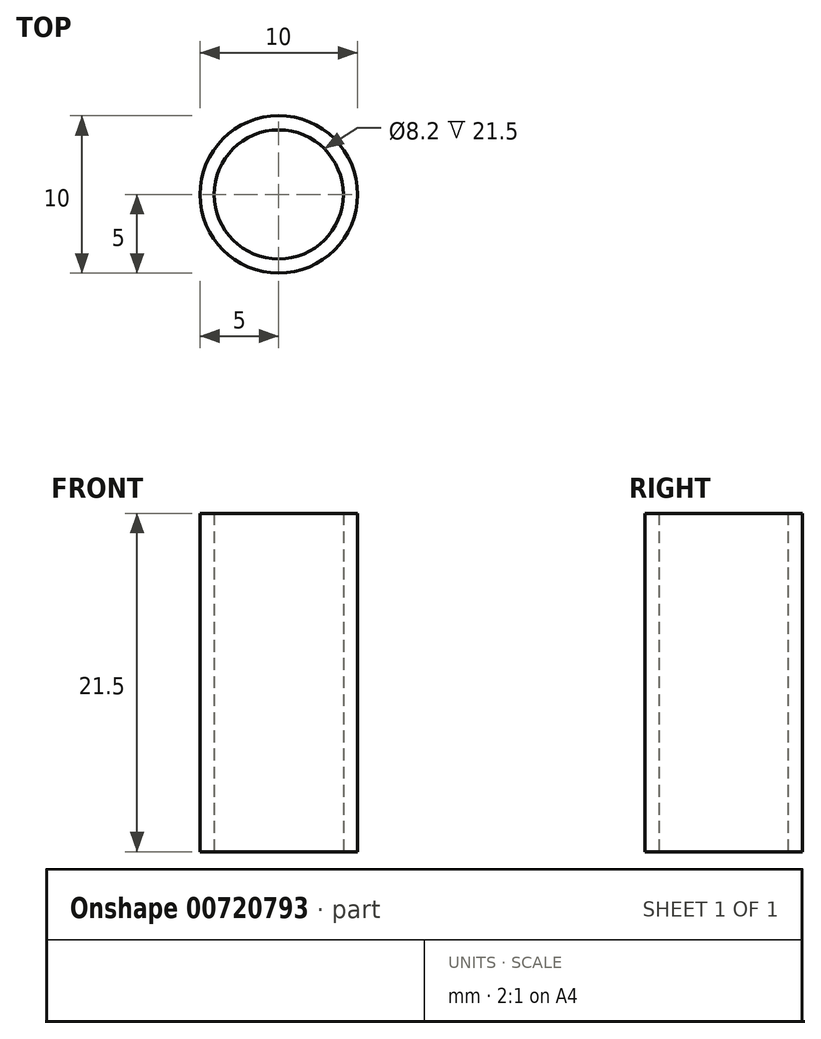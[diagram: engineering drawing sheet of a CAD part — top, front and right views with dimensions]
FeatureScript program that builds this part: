
annotation { "Feature Type Name" : "Feature", "Feature Type Description" : "" }
export const myFeature = defineFeature(function(context is Context, id is Id, definition is map)
    precondition{}
    {
        {
            var Q0;
            Q0=qCreatedBy(makeId("Top.planeOp"),FACE);
            var sketch = newSketch(context, id + "F0", { "sketchPlane" : qUnion([Q0])});
            skCircle(sketch, "E0", {"center": v(0, 0) * mm, "radius": 4.1 * mm});
            skCircle(sketch, "E1", {"center": v(0, 0) * mm, "radius": 5 * mm});
            skSolve(sketch);
        }
        {
            var Q0;
            Q0=makeQuery(id+"F0.imprint","IMPRINT",FACE,{"disambiguationData":[TD([[makeQuery(id+"F0.imprint","IMPRINT",EDGE,{"derivedFrom":sQuery(id+"F0.wireOp",EDGE,"E0")}),-1.0]])]});
            extrude(context, id + "F1", {"entities" : qUnion([Q0]), "depth" : 21.5 * mm, "offsetDistance" : 25 * mm});
        }
    });
